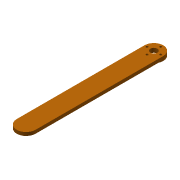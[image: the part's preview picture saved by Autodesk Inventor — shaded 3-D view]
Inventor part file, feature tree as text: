
AUTODESK INVENTOR PART (.ipt)
format: ipt  version: 2016 (Build 200138000, 138)  size: 111,616 bytes
history: native  units: mm
features: sketch x4, extrude x3, reference x3, other x1, hole x1
ambient origin geometry x8: Origin, YZ Plane, XZ Plane, XY Plane, X Axis, Y Axis, Z Axis, Center Point
bodies: Solid1 (feature_tree)
feature tree (12):
  other  "skeleton.ipt"
  extrude  "Extrusion1"  Depth=1.0mm TaperAngle=0.0deg
  extrude  "Extrusion2"  Depth=4.0mm TaperAngle=0.0deg
  hole  "Hole1"  [1 undecoded]
  extrude  "Extrusion3"  [1 undecoded]
  sketch  "Sketch1"  dims[d0=10.0mm d1=1.0mm d2=0.0mm]
  reference  "Reference1"
  sketch  "Sketch2"  dims[d3=60.0mm d4=4.0mm d5=0.0mm]
  sketch  "Sketch3"  dims[d6=2.6mm d7=6.0mm d8=4.0mm d9=2.0mm d10=90.0deg d11=8.0mm d12=20.594885mm d13=1.0mm]
  reference  "Reference2"
  sketch  "Sketch4"  dims[d14=4.0mm d15=0.0mm]
  reference  "Reference3"
note: 2 required parameter values undecoded (feature->parameter linkage not recoverable at this tier; creation-order binding heuristic only, values carry confidence <= 0.55)
